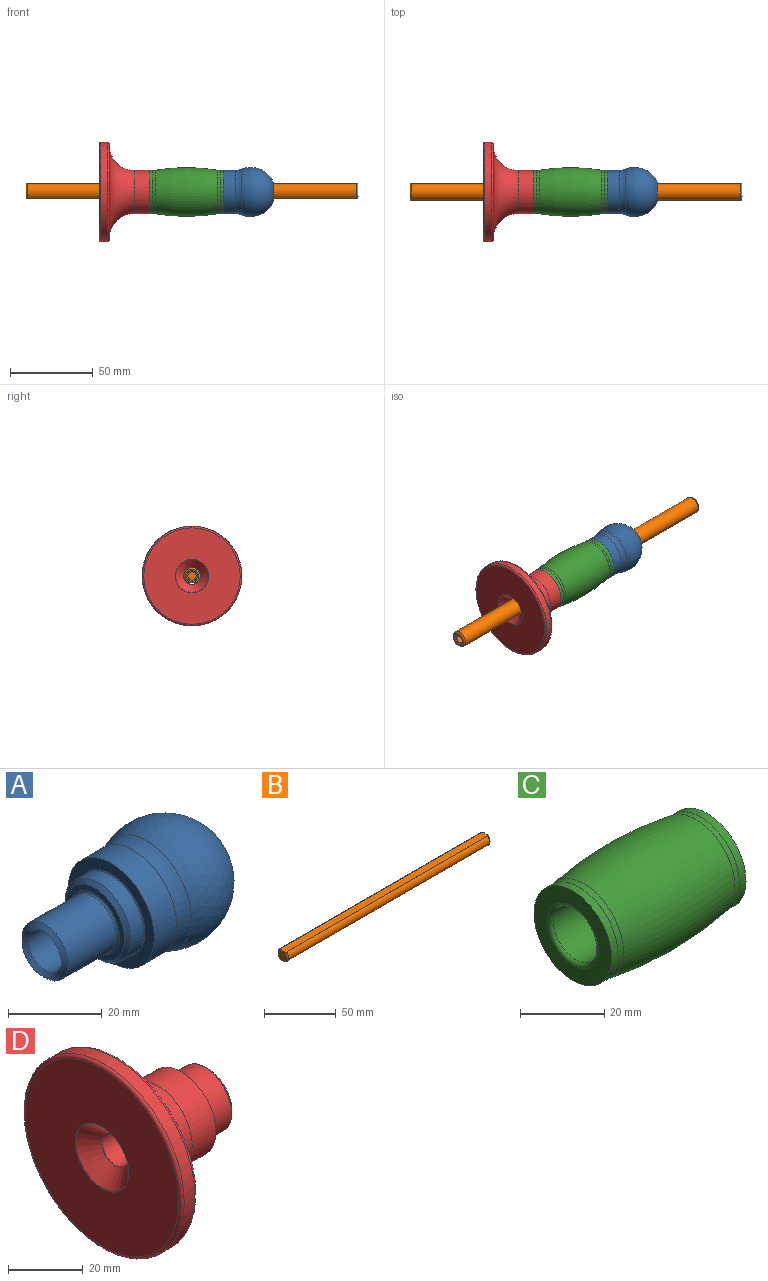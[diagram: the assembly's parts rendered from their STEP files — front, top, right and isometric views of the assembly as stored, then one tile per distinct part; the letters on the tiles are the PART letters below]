
ASSEMBLY  parts=4 mates=3
PART A: 14 faces, bbox 50.9x34.4x34.4 mm
  f0: cylinder r=5mm len=49.4mm, axis (-1,0,0), area 1552.1mm2, adj f8,f10
  f1: sphere r=14.84mm, area 1800.9mm2, adj f10,f12
  f2: cylinder r=13mm len=26mm, axis (-1,0,0), area 553.3mm2, adj f3,f12
  f3: plane 26x26mm, normal (-1,0,0), area 204.1mm2, adj f2,f13
  f4: cylinder r=10mm len=20mm, axis (-1,0,0), area 238.8mm2, adj f7,f13
  f5: plane 18x18mm, normal (-1,0,0), area 77.8mm2, adj f7,f11
  f6: cylinder r=7mm len=14.5mm, axis (-1,0,0), area 637.7mm2, adj f9,f11
  f7: cone r=9mm half-angle=45deg, axis (1,0,0), area 84.4mm2, adj f4,f5
  f8: cone r=5mm half-angle=45deg, axis (-1,0,0), area 48.9mm2, adj f0,f9
  f9: cone r=6mm half-angle=45deg, axis (1,0,0), area 57.8mm2, adj f6,f8
  f10: torus R=5.5mm, axis (-1,0,0), area 32.5mm2, adj f0,f1
  f11: torus R=7.5mm, axis (-1,0,0), area 35.4mm2, adj f5,f6
  f12: torus R=23mm, axis (1,0,0), area 322.5mm2, adj f1,f2
  f13: torus R=10.2mm, axis (-1,0,0), area 19.9mm2, adj f3,f4
PART B: 17 faces, bbox 200x10.8x10.7 mm
  f0: cylinder r=5mm len=198mm, axis (1,0,0), area 4932.8mm2, adj f5,f6,f11,f14
  f1: plane 8x7.9mm, normal (-1,0,0), area 50.1mm2, adj f6,f15
  f2: plane 8x7.9mm, normal (1,0,0), area 17mm2, adj f5,f8,f10
  f3: cylinder r=2.5mm len=24.25mm, axis (1,0,0), area 380.9mm2, adj f4,f8
  f4: plane 5x5mm, normal (1,0,0), area 19.6mm2, adj f3
  f5: torus R=4mm, axis (1,0,0), area 37.9mm2, adj f0,f2,f9,f12
  f6: torus R=4mm, axis (1,0,0), area 37.9mm2, adj f0,f1,f13,f16
  f7: plane 199.8x5.93mm, normal (0,0,1), area 1184.1mm2, adj f9,f10,f11,f12,f13,f14,f15,f16
  f8: cone r=2.5mm half-angle=45deg, axis (1,0,0), area 19.2mm2, adj f2,f3
  f9: bspline ~2.74x1.05mm, area 0.3mm2, adj f5,f7,f10,f11
  f10: cylinder r=0.1mm len=1.78mm, axis (0,-1,0), area 0.3mm2, adj f2,f7,f9,f12
  f11: cylinder r=0.1mm len=198mm, axis (1,0,0), area 12.9mm2, adj f0,f7,f9,f13
  f12: bspline ~2.74x1.17mm, area 0.3mm2, adj f5,f7,f10,f14
  f13: bspline ~2.74x1.17mm, area 0.3mm2, adj f6,f7,f11,f15
  f14: cylinder r=0.1mm len=198mm, axis (1,0,0), area 12.9mm2, adj f0,f7,f12,f16
  f15: cylinder r=0.1mm len=1.78mm, axis (0,-1,0), area 0.3mm2, adj f1,f7,f13,f16
  f16: bspline ~2.74x1.05mm, area 0.3mm2, adj f6,f7,f14,f15
PART C: 10 faces, bbox 50x34.4x34.4 mm
  f0: plane 26x26mm, normal (-1,0,0), area 303.9mm2, adj f1,f7
  f1: torus R=8.5mm, axis (-1,0,0), area 77.6mm2, adj f0,f2
  f2: cylinder r=7.5mm len=43mm, axis (-1,0,0), area 2026.3mm2, adj f1,f3
  f3: torus R=8.5mm, axis (-1,0,0), area 77.6mm2, adj f2,f4
  f4: plane 26x26mm, normal (1,0,0), area 303.9mm2, adj f3,f5
  f5: cylinder r=13mm len=26mm, axis (-1,0,0), area 175.5mm2, adj f4,f8
  f6: revolved ~37.39x29.4mm, area 3346.1mm2, adj f8,f9
  f7: cylinder r=13mm len=26mm, axis (-1,0,0), area 175.5mm2, adj f0,f9
  f8: torus R=23mm, axis (-1,0,0), area 136.4mm2, adj f5,f6
  f9: torus R=23mm, axis (-1,0,0), area 136.4mm2, adj f6,f7
PART D: 26 faces, bbox 40x64.9x64.9 mm
  f0: plane 58x58mm, normal (-1,0,0), area 2321.4mm2, adj f12,f17
  f1: cylinder r=5mm len=13.79mm, axis (-1,0,0), area 433.3mm2, adj f18,f23
  f2: plane 14x14mm, normal (1,0,0), area 36.9mm2, adj f3,f24
  f3: cylinder r=7mm len=18.9mm, axis (-1,0,0), area 831.1mm2, adj f2,f20
  f4: plane 17.79x17.79mm, normal (1,0,0), area 42.3mm2, adj f21,f22
  f5: cylinder r=10mm len=20mm, axis (-1,0,0), area 543.3mm2, adj f19,f25
  f6: plane 26x26mm, normal (1,0,0), area 200.9mm2, adj f7,f25
  f7: cylinder r=13mm len=26mm, axis (-1,0,0), area 735.1mm2, adj f6,f8
  f8: torus R=28mm, axis (-1,0,0), area 2731.5mm2, adj f7,f9
  f9: plane 58x58mm, normal (1,0,0), area 179.1mm2, adj f8,f11
  f10: cylinder r=30mm len=60mm, axis (-1,0,0), area 754mm2, adj f11,f12
  f11: torus R=29mm, axis (1,0,0), area 292.5mm2, adj f9,f10
  f12: torus R=29mm, axis (-1,0,0), area 292.5mm2, adj f0,f10
  f13: cone r=6mm half-angle=45deg, axis (1,0,0), area 41.7mm2, adj f23,f24
  f14: cone r=8mm half-angle=45deg, axis (1,0,0), area 56.9mm2, adj f20,f21
  f15: cone r=10mm half-angle=45deg, axis (-1,0,0), area 72.1mm2, adj f19,f22
  f16: cone r=5mm half-angle=45deg, axis (-1,0,0), area 323.5mm2, adj f17,f18
  f17: torus R=10.1mm, axis (-1,0,0), area 12.3mm2, adj f0,f16
  f18: torus R=5.25mm, axis (1,0,0), area 6.2mm2, adj f1,f16
  f19: torus R=9.75mm, axis (1,0,0), area 12.3mm2, adj f5,f15
  f20: torus R=7.25mm, axis (-1,0,0), area 8.7mm2, adj f3,f14
  f21: torus R=8.1mm, axis (-1,0,0), area 9.9mm2, adj f4,f14
  f22: torus R=8.9mm, axis (-1,0,0), area 11.1mm2, adj f4,f15
  f23: torus R=5.25mm, axis (-1,0,0), area 6.2mm2, adj f1,f13
  f24: torus R=6.1mm, axis (-1,0,0), area 7.4mm2, adj f2,f13
  f25: torus R=10.25mm, axis (-1,0,0), area 24.9mm2, adj f5,f6
PLACE A t=(378.76,54.19,59.91)mm
PLACE B rot(axis=(0,1,0),180deg) t=(280.62,54.19,59.91)mm
PLACE C t=(354.76,54.19,59.91)mm
PLACE D t=(324.76,54.19,59.91)mm
MATE fastened C.f1 <-> A.f11  axis (1,0,0) through (399.76,54.19,59.91)mm
MATE fastened C.f1 <-> D.f1  axis (-1,0,0) through (354.76,54.19,59.91)mm
MATE slider B.f0 <-> D.f1  axis (-1,0,0) through (280.62,54.19,59.91)mm
